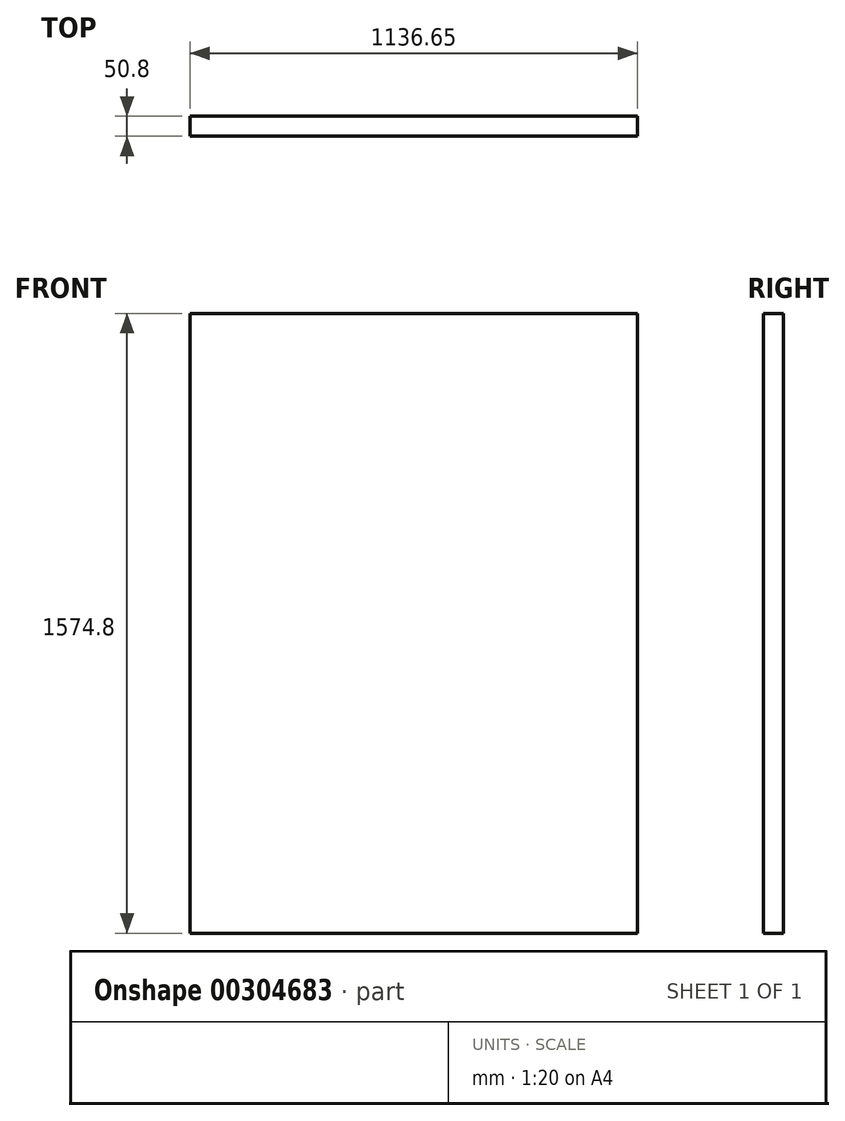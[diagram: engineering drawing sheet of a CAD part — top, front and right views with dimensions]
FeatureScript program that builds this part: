
annotation { "Feature Type Name" : "Feature", "Feature Type Description" : "" }
export const myFeature = defineFeature(function(context is Context, id is Id, definition is map)
    precondition{}
    {
        {
            var Q0;
            Q0=qCreatedBy(makeId("Front.planeOp"),FACE);
            var sketch = newSketch(context, id + "F0", { "sketchPlane" : qUnion([Q0])});
            skLineSegment(sketch, "E0.bottom", {"start": v(-561.61, 925.72) * mm, "end": v(575.04, 925.72) * mm});
            skLineSegment(sketch, "E0.top", {"start": v(-561.61, -649.08) * mm, "end": v(575.04, -649.08) * mm});
            skLineSegment(sketch, "E0.left", {"start": v(-561.61, 925.72) * mm, "end": v(-561.61, -649.08) * mm});
            skLineSegment(sketch, "E0.right", {"start": v(575.04, 925.72) * mm, "end": v(575.04, -649.08) * mm});
            skSolve(sketch);
        }
        {
            var Q0;
            Q0=makeQuery(id+"F0.imprint","IMPRINT",FACE,{"disambiguationData":[TD([[makeQuery(id+"F0.imprint","IMPRINT",EDGE,{"derivedFrom":sQuery(id+"F0.wireOp",EDGE,"E0.bottom")}),-1.0]])]});
            extrude(context, id + "F1", {"entities" : qUnion([Q0]), "depth" : 50.8 * mm});
        }
    });
